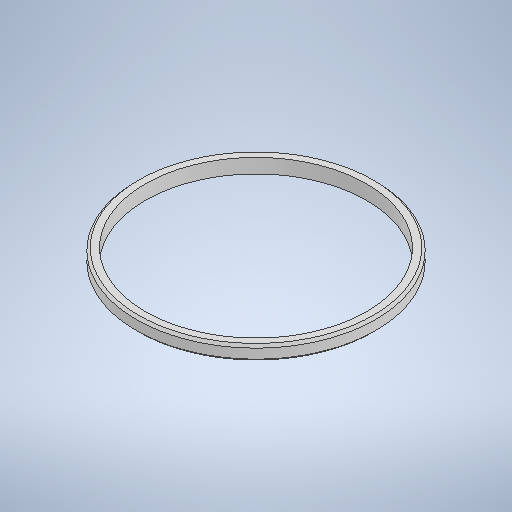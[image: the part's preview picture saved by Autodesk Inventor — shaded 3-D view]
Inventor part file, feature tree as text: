
AUTODESK INVENTOR PART (.ipt)
format: ipt  version: 2025.1 (Build 291241000, 241)  size: 263,680 bytes
history: native  units: mm
features: extrude x1, chamfer x1, sketch x1
ambient origin geometry x8: Origin, YZ Plane, XZ Plane, XY Plane, X Axis, Y Axis, Z Axis, Center Point
bodies: Solid1 (feature_tree)
feature tree (3):
  extrude  "Extrusion1"  Depth=12.0mm
  chamfer  "Chamfer1"  Distance=12.0mm
  sketch  "Sketch1"  dims[d0=200.0mm d1=185.0mm d2=12.0mm d3=0.0mm d4=2.0mm d5=2.0mm d6=45.0deg]
